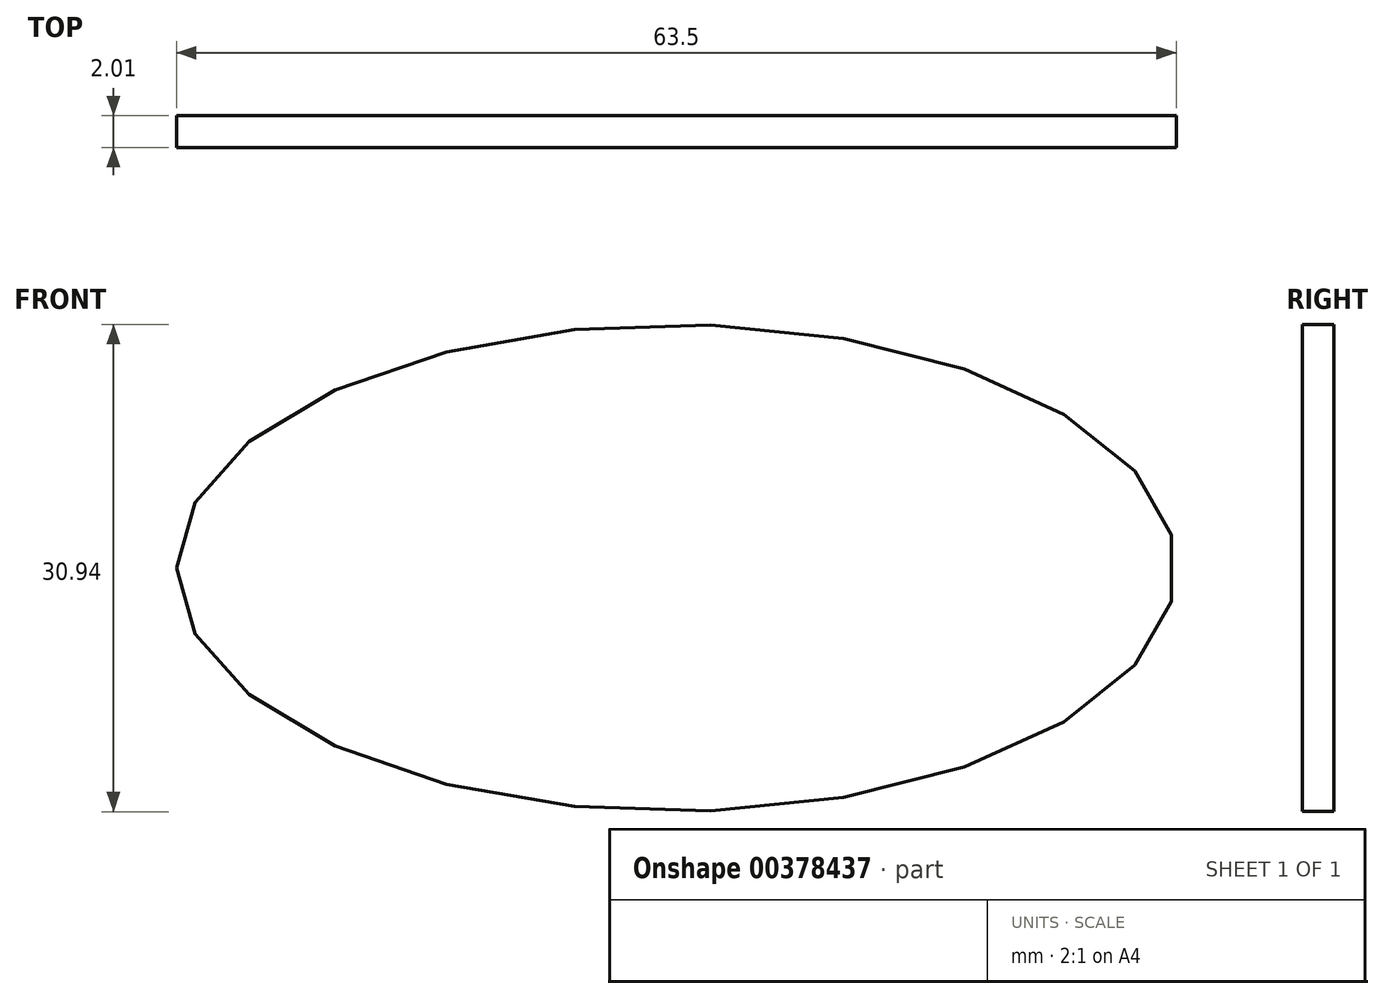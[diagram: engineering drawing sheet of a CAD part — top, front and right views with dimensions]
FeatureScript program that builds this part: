
annotation { "Feature Type Name" : "Feature", "Feature Type Description" : "" }
export const myFeature = defineFeature(function(context is Context, id is Id, definition is map)
    precondition{}
    {
        {
            var Q0;
            Q0=qCreatedBy(makeId("Front.planeOp"),FACE);
            var sketch = newSketch(context, id + "F0", { "sketchPlane" : qUnion([Q0])});
            skEllipse(sketch, "E0", {"center": v(0, 0) * mm, "majorRadius": 31.75 * mm, "minorRadius": 15.47 * mm, "majorAxis": v(-1, 0)});
            skSolve(sketch);
        }
        {
            var Q0;
            Q0=makeQuery(id+"F0.imprint","IMPRINT",FACE,{"disambiguationData":[TD([[makeQuery(id+"F0.imprint","IMPRINT",EDGE,{"derivedFrom":sQuery(id+"F0.wireOp",EDGE,"E0")}),1.0]])]});
            var Q1;
            Q1 = qConstructionFilter(qBodyType(qCreatedBy(id + "F0" ,EDGE), BodyType.WIRE), ConstructionObject.NO);
            extrude(context, id + "F1", {"entities" : qUnion([Q0]), "surfaceEntities" : qUnion([Q1]), "depth" : 2 * mm});
        }
        {
            var Q0;
            Q0=makeQuery(id+"F0.imprint","IMPRINT",FACE,{"disambiguationData":[TD([[makeQuery(id+"F0.imprint","IMPRINT",EDGE,{"derivedFrom":sQuery(id+"F0.wireOp",EDGE,"E0")}),1.0]])]});
            var Q1;
            Q1=sQuery(id+"F0.wireOp",EDGE,"E0");
            extrude(context, id + "F2", {"entities" : qUnion([Q0]), "bodyType" : ToolBodyType.SURFACE, "surfaceEntities" : qUnion([Q1]), "depth" : 4 * mm});
        }
    });
